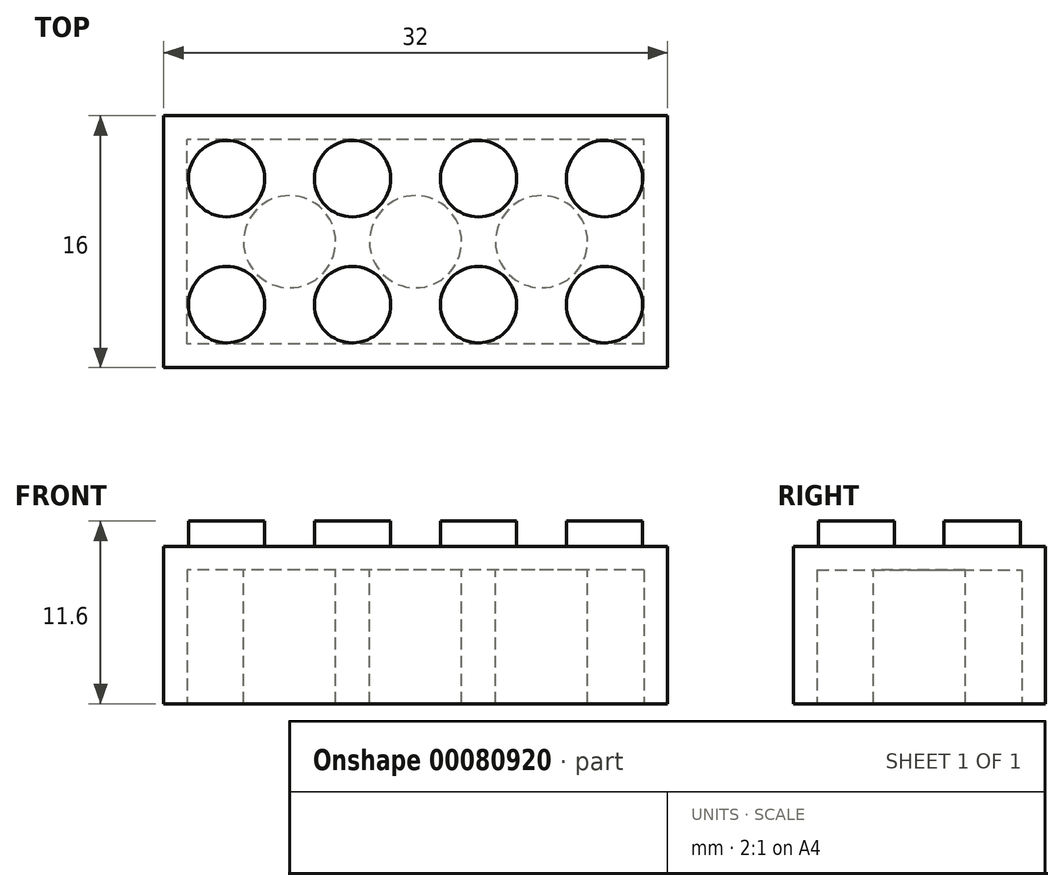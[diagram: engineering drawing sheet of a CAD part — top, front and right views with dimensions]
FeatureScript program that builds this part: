
annotation { "Feature Type Name" : "Feature", "Feature Type Description" : "" }
export const myFeature = defineFeature(function(context is Context, id is Id, definition is map)
    precondition{}
    {
        {
            var Q0;
            Q0=qCreatedBy(makeId("Top.planeOp"),FACE);
            var sketch = newSketch(context, id + "F0", { "sketchPlane" : qUnion([Q0])});
            skLineSegment(sketch, "E0.bottom", {"start": v(16, -8) * mm, "end": v(-16, -8) * mm});
            skLineSegment(sketch, "E0.top", {"start": v(16, 8) * mm, "end": v(-16, 8) * mm});
            skLineSegment(sketch, "E0.left", {"start": v(16, -8) * mm, "end": v(16, 8) * mm});
            skLineSegment(sketch, "E0.right", {"start": v(-16, -8) * mm, "end": v(-16, 8) * mm});
            skPoint(sketch, "E0.middle", {"position": v(0, 0) * mm});
            skSolve(sketch);
        }
        {
            var Q0;
            Q0 = qSketchRegion(id + "F0", true);
            extrude(context, id + "F1", {"entities" : qUnion([Q0]), "depth" : 10 * mm});
        }
        {
            var Q0;
            Q0=makeQuery(id+"F1.opExtrude","CAP_FACE",FACE,{"disambiguationData":[OSD([sQuery(id+"F0.wireOp",EDGE,"E0.bottom"),sQuery(id+"F0.wireOp",EDGE,"E0.top"),sQuery(id+"F0.wireOp",EDGE,"E0.left"),sQuery(id+"F0.wireOp",EDGE,"E0.right")])],"isStart":true});
            shell(context, id + "F2", {"entities" : qUnion([Q0]), "thickness" : 1.5 * mm});
        }
        {
            var Q0;
            Q0=makeQuery(id+"F1.opExtrude","CAP_FACE",FACE,{"disambiguationData":[OSD([sQuery(id+"F0.wireOp",EDGE,"E0.bottom"),sQuery(id+"F0.wireOp",EDGE,"E0.top"),sQuery(id+"F0.wireOp",EDGE,"E0.left"),sQuery(id+"F0.wireOp",EDGE,"E0.right")])],"isStart":false});
            var sketch = newSketch(context, id + "F3", { "sketchPlane" : qUnion([Q0])});
            skCircle(sketch, "E1", {"center": v(-12, -4) * mm, "radius": 2.43 * mm});
            skCircle(sketch, "E2.0.1.0", {"center": v(-12, 4) * mm, "radius": 2.43 * mm});
            skCircle(sketch, "E2.1.0.0", {"center": v(-4, -4) * mm, "radius": 2.43 * mm});
            skCircle(sketch, "E2.1.1.0", {"center": v(-4, 4) * mm, "radius": 2.43 * mm});
            skCircle(sketch, "E2.2.0.0", {"center": v(4, -4) * mm, "radius": 2.43 * mm});
            skCircle(sketch, "E2.2.1.0", {"center": v(4, 4) * mm, "radius": 2.43 * mm});
            skCircle(sketch, "E2.3.0.0", {"center": v(12, -4) * mm, "radius": 2.43 * mm});
            skCircle(sketch, "E2.3.1.0", {"center": v(12, 4) * mm, "radius": 2.43 * mm});
            skLineSegment(sketch, "E2.direction1", {"start": v(-12, -4) * mm, "end": v(-4, -4) * mm, "construction": true});
            skLineSegment(sketch, "E2.direction2", {"start": v(-12, -4) * mm, "end": v(-12, 4) * mm, "construction": true});
            skSolve(sketch);
        }
        {
            var Q0;
            Q0 = qSketchRegion(id + "F3", true);
            extrude(context, id + "F4", {"entities" : qUnion([Q0]), "operationType" : NewBodyOperationType.ADD, "depth" : 1.6 * mm});
        }
        {
            var Q0;
            Q0=makeQuery(id+"F1.opExtrude","CAP_FACE",FACE,{"disambiguationData":[OSD([sQuery(id+"F0.wireOp",EDGE,"E0.bottom"),sQuery(id+"F0.wireOp",EDGE,"E0.top"),sQuery(id+"F0.wireOp",EDGE,"E0.left"),sQuery(id+"F0.wireOp",EDGE,"E0.right")])],"isStart":false});
            var sketch = newSketch(context, id + "F5", { "sketchPlane" : qUnion([Q0])});
            skCircle(sketch, "E3", {"center": v(-8, 0) * mm, "radius": 2.93 * mm});
            skCircle(sketch, "E4", {"center": v(0, 0) * mm, "radius": 2.93 * mm});
            skCircle(sketch, "E5", {"center": v(8, 0) * mm, "radius": 2.93 * mm});
            skSolve(sketch);
        }
        {
            var Q0;
            Q0 = qSketchRegion(id + "F5", true);
            extrude(context, id + "F6", {"entities" : qUnion([Q0]), "operationType" : NewBodyOperationType.ADD, "oppositeDirection" : true, "depth" : 10 * mm});
        }
    });
